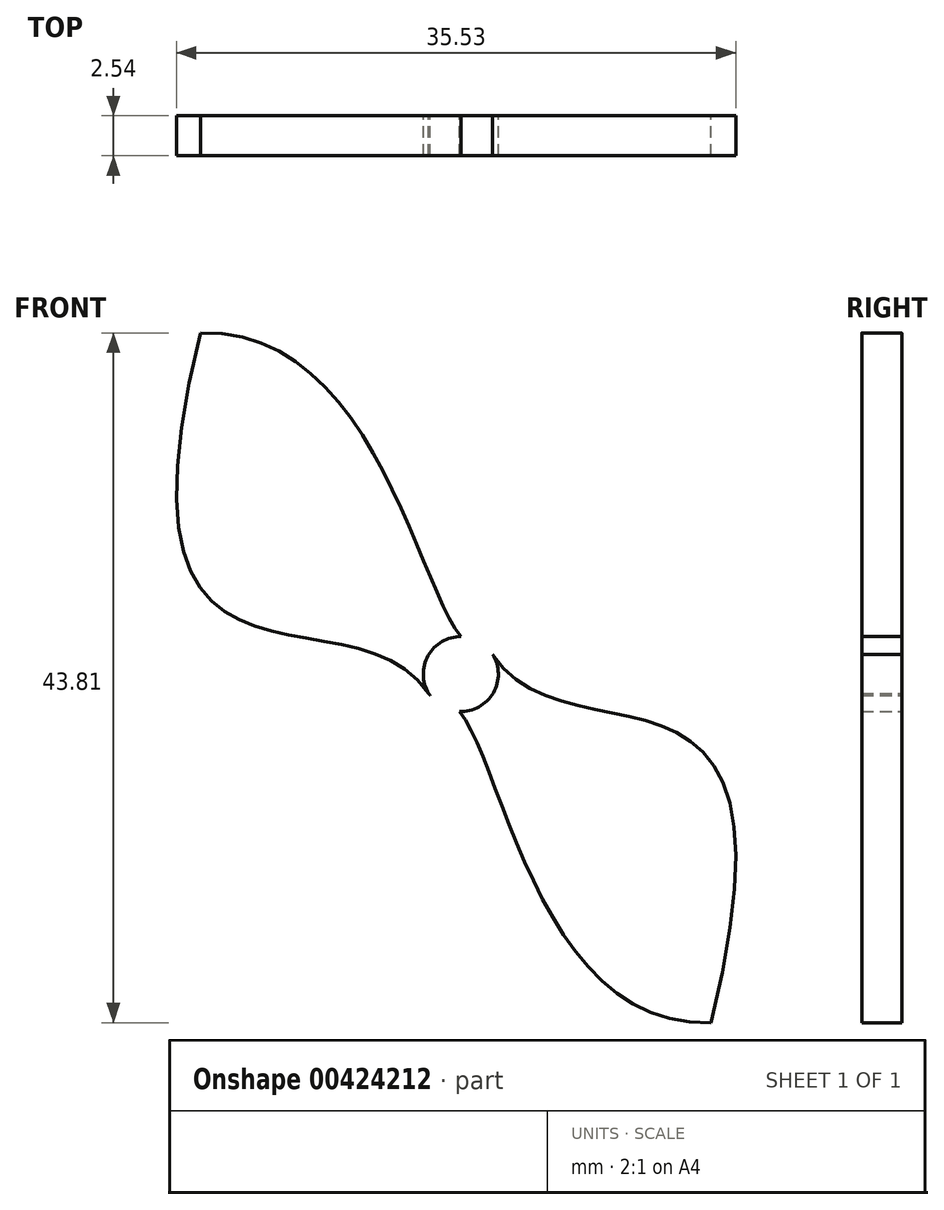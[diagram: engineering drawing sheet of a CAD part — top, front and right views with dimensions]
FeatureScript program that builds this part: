
annotation { "Feature Type Name" : "Feature", "Feature Type Description" : "" }
export const myFeature = defineFeature(function(context is Context, id is Id, definition is map)
    precondition{}
    {
        {
            var Q0;
            Q0=qCreatedBy(makeId("Front.planeOp"),FACE);
            var sketch = newSketch(context, id + "F0", { "sketchPlane" : qUnion([Q0])});
            skCircle(sketch, "E0", {"center": v(-18.04, 19.46) * mm, "radius": 2.38 * mm});
            skCircle(sketch, "E1", {"center": v(-18.04, 19.46) * mm, "radius": 1.59 * mm});
            skFitSpline(sketch, "E2", {"points": [v(-18.04, 21.84) * mm, v(-34.57, 41.12) * mm], "startDerivative": vector(-8.5, 10.53) * mm, "endDerivative": vector(-32.58, -1.1) * mm});
            skFitSpline(sketch, "E3", {"points": [v(-34.57, 41.12) * mm, v(-19.98, 18.09) * mm], "startDerivative": vector(-19.65, -78.49) * mm, "endDerivative": vector(14.59, -23.03) * mm});
            skFitSpline(sketch, "E4", {"points": [v(-18.12, 17.08) * mm, v(-2.15, -2.68) * mm], "startDerivative": vector(8.5, -10.53) * mm, "endDerivative": vector(32.58, 1.1) * mm});
            skFitSpline(sketch, "E5", {"points": [v(-2.15, -2.68) * mm, v(-16.04, 20.76) * mm], "startDerivative": vector(19.65, 78.49) * mm, "endDerivative": vector(-14.59, 23.03) * mm});
            skSolve(sketch);
        }
        {
            var Q0;
            {var subQ0=sQuery(id+"F0.wireOp",EDGE,"E2");Q0=makeQuery(id+"F0.imprint","IMPRINT",FACE,{"disambiguationData":[TD([[makeQuery(id+"F0.imprint","IMPRINT",EDGE,{"derivedFrom":subQ0}),1.0]])]});}
            var Q1;
            {var subQ0=sQuery(id+"F0.wireOp",EDGE,"E3");var subQ1=sQuery(id+"F0.wireOp",EDGE,"E0");var subQ2=makeQuery(id+"F0.imprint","INTERSECT",VERTEX,{"disambiguationData":[OD(0.0)],"derivedFrom":[subQ1,subQ0]});Q1=makeQuery(id+"F0.imprint","IMPRINT",FACE,{"disambiguationData":[TD([[makeQuery(id+"F0.imprint","IMPRINT",EDGE,{"disambiguationData":[TD([[subQ2,1.0]])],"derivedFrom":subQ1}),1.0]])]});}
            var Q2;
            {var subQ0=sQuery(id+"F0.wireOp",EDGE,"E4");Q2=makeQuery(id+"F0.imprint","IMPRINT",FACE,{"disambiguationData":[TD([[makeQuery(id+"F0.imprint","IMPRINT",EDGE,{"derivedFrom":subQ0}),1.0]])]});}
            extrude(context, id + "F1", {"entities" : qUnion([Q0, Q1, Q2]), "depth" : 2.54 * mm});
        }
    });
